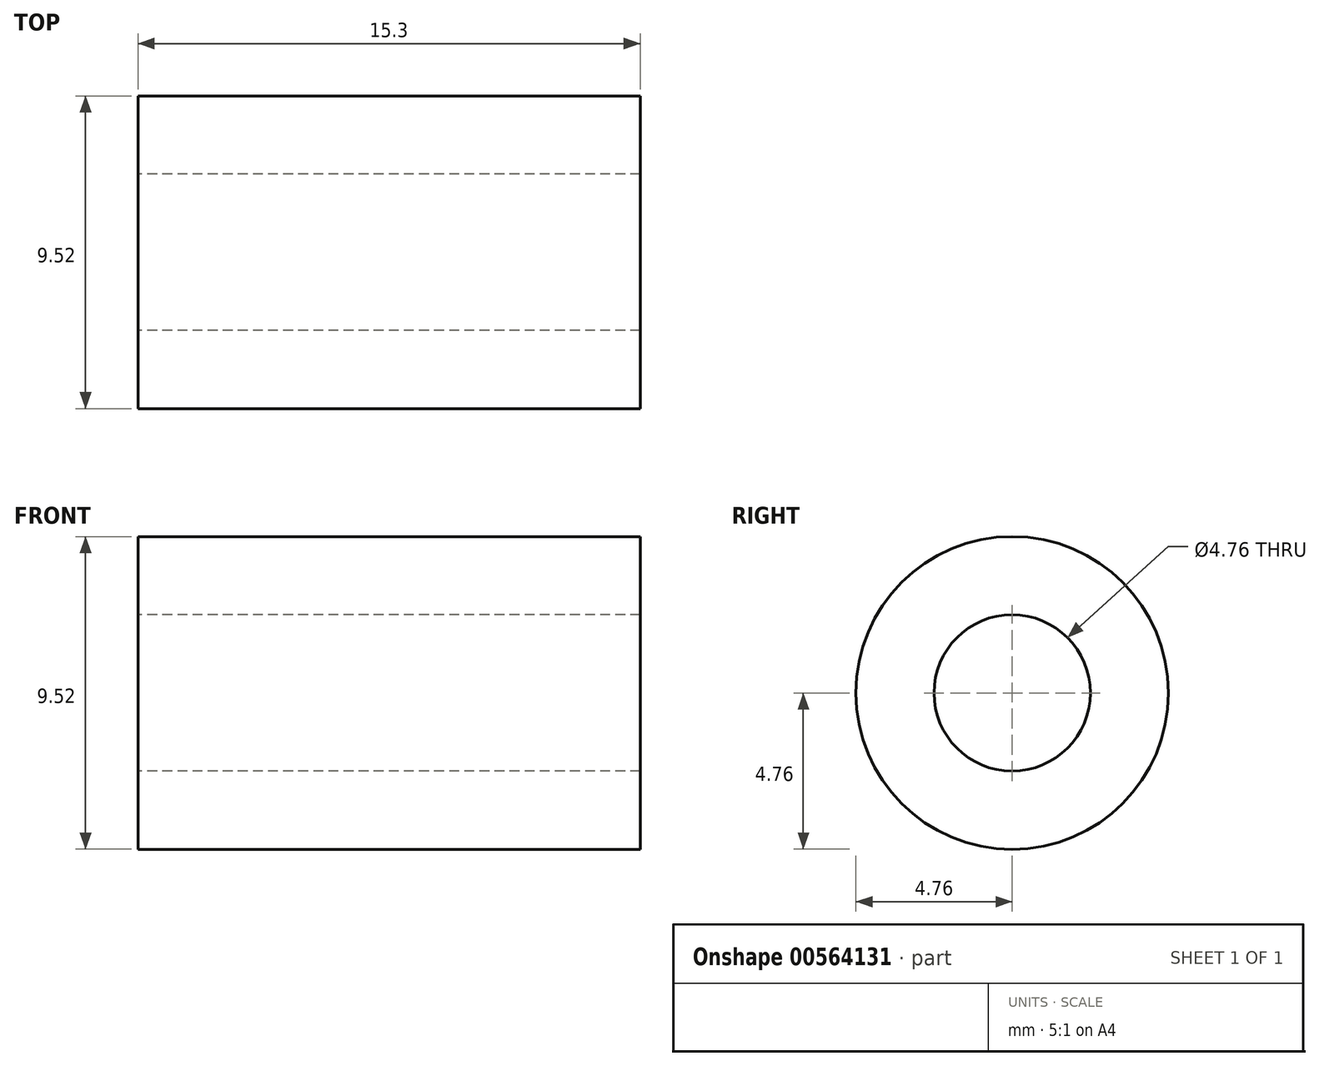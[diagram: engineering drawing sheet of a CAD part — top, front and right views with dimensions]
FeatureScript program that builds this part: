
annotation { "Feature Type Name" : "Feature", "Feature Type Description" : "" }
export const myFeature = defineFeature(function(context is Context, id is Id, definition is map)
    precondition{}
    {
        {
            var Q0;
            Q0=qCreatedBy(makeId("Right.planeOp"),FACE);
            var sketch = newSketch(context, id + "F0", { "sketchPlane" : qUnion([Q0])});
            skCircle(sketch, "E0", {"center": v(0, 0) * mm, "radius": 4.76 * mm});
            skCircle(sketch, "E1", {"center": v(0, 0) * mm, "radius": 2.38 * mm});
            skSolve(sketch);
        }
        {
            var Q0;
            Q0 = qSketchRegion(id + "F0", true);
            extrude(context, id + "F1", {"entities" : qUnion([Q0]), "depth" : 14.29 * mm + 1.02 * mm, "offsetDistance" : 25.4 * mm});
        }
    });
